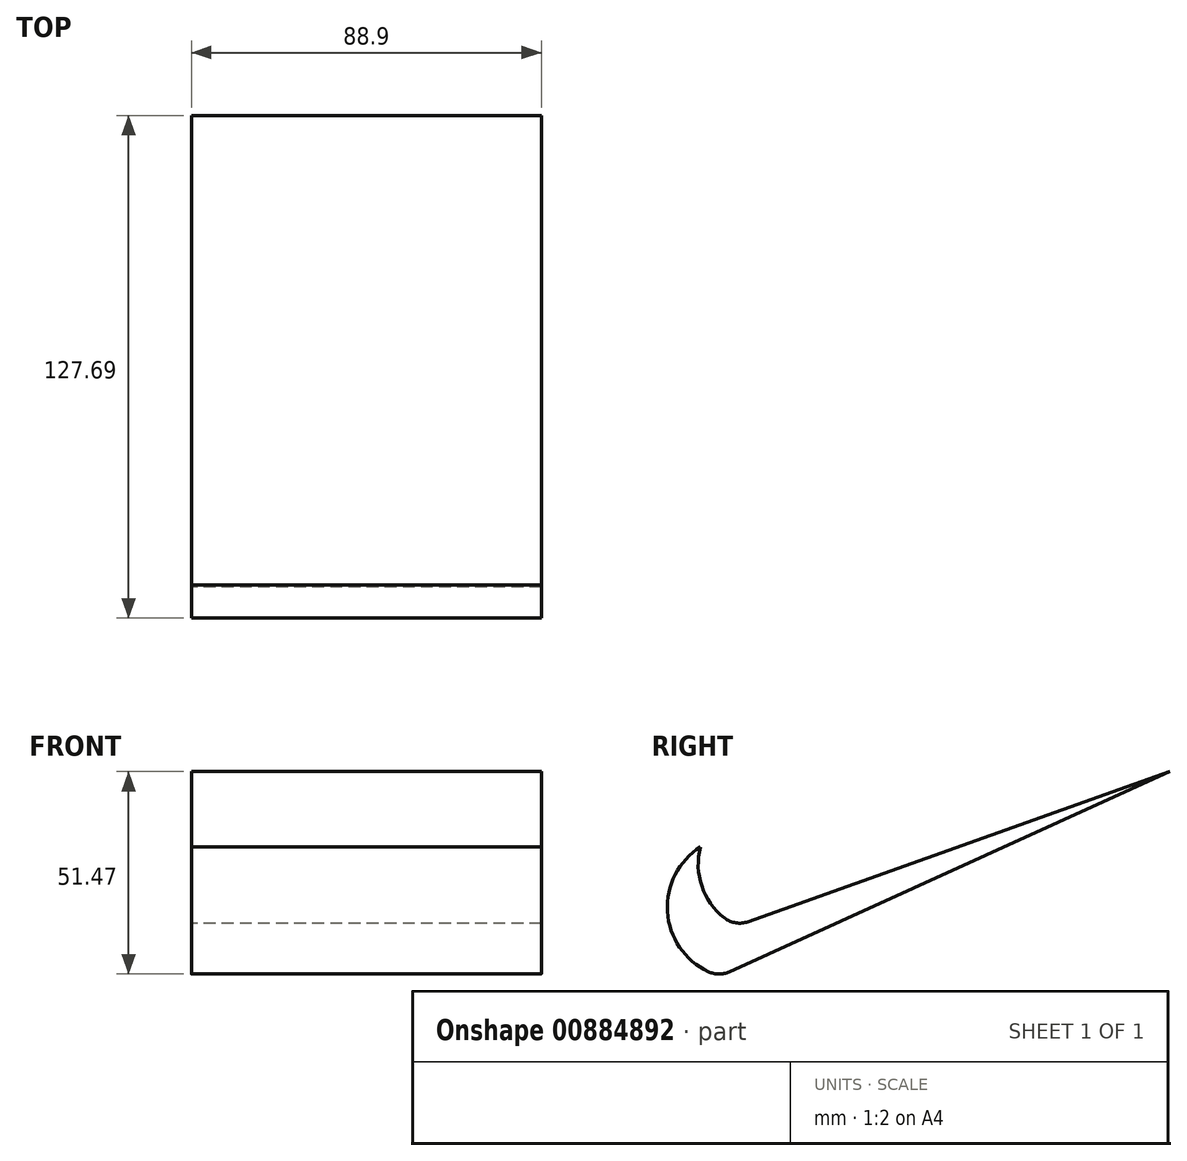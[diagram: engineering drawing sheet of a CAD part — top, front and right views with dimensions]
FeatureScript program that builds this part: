
annotation { "Feature Type Name" : "Feature", "Feature Type Description" : "" }
export const myFeature = defineFeature(function(context is Context, id is Id, definition is map)
    precondition{}
    {
        {
            var Q0;
            Q0=qCreatedBy(makeId("Right.planeOp"),FACE);
            var sketch = newSketch(context, id + "F0", { "sketchPlane" : qUnion([Q0])});
            skArc(sketch, "E0", {"start": v(-38.77, 33.53) * mm, "mid": v(-47.17, 17.09) * mm, "end": v(-36.8, 1.8) * mm});
            skLineSegment(sketch, "E1", {"start": v(-31.47, 1.77) * mm, "end": v(80.49, 52.67) * mm});
            skLineSegment(sketch, "E2", {"start": v(80.49, 52.67) * mm, "end": v(-26.66, 14.5) * mm});
            skArc(sketch, "E3", {"start": v(-38.77, 33.53) * mm, "mid": v(-38.47, 23.56) * mm, "end": v(-32.66, 15.44) * mm});
            skPoint(sketch, "E4.visualSharp", {"position": v(-29.46, 13.5) * mm});
            skArc(sketch, "E4.filletArc", {"start": v(-32.66, 15.44) * mm, "mid": v(-29.78, 14.2) * mm, "end": v(-26.66, 14.5) * mm});
            skPoint(sketch, "E5.visualSharp", {"position": v(-33.8, 0.7) * mm});
            skArc(sketch, "E5.filletArc", {"start": v(-36.8, 1.8) * mm, "mid": v(-34.14, 1.2) * mm, "end": v(-31.47, 1.77) * mm});
            skSolve(sketch);
        }
        {
            var Q0;
            Q0 = qSketchRegion(id + "F0", true);
            extrude(context, id + "F1", {"entities" : qUnion([Q0]), "depth" : 88.9 * mm, "offsetDistance" : 25.4 * mm});
        }
    });
